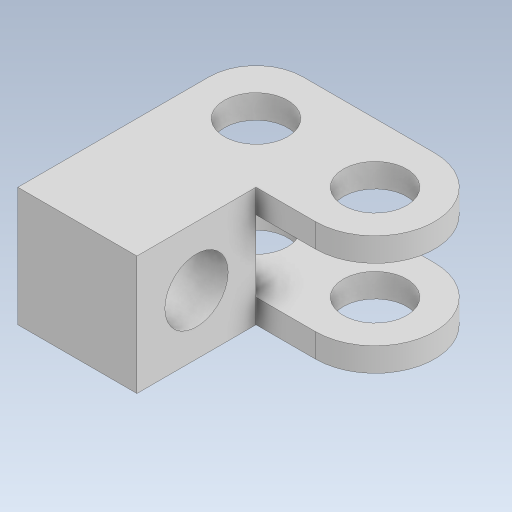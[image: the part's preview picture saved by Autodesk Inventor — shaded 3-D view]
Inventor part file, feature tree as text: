
AUTODESK INVENTOR PART (.ipt)
format: ipt  version: 2023 (Build 270158000, 158)  size: 164,864 bytes
history: native  units: in
note: dims shown in document units (in); Inventor stores cm internally (conversion verified against a paired STEP export)
features: sketch x4, extrude x2, hole x2, plane x1, fillet x1
ambient origin geometry x8: Origin, YZ Plane, XZ Plane, XY Plane, X Axis, Y Axis, Z Axis, Center Point
bodies: Solid1 (feature_tree)
feature tree (10):
  extrude  "Extrusion1"  Depth=1.0in
  sketch  "Sketch2"  dims[d2=1.0in d3=0.5in]
  extrude  "Extrusion2"  Depth=0.5in
  hole  "Hole2"  [1 undecoded]
  hole  "Hole3"  [1 undecoded]
  plane  "Work Plane1"
  fillet  "Fillet1"  [1 undecoded]
  sketch  "Sketch1"  dims[d0=0.5in d1=1.0in]
  sketch  "Sketch3"  dims[d4=0.5in d5=0.0in d6=0.25in]
  sketch  "Sketch4"  dims[d15=0.3in d16=0.5in d17=0.0in d18=0.266in d19=0.75in d20=0.375in d21=0.25in d22=0.5635in d23=0.5in d24=0.8108in d25=0.266in d26=0.75in d27=0.375in d28=0.25in d29=0.5635in d30=0.5in d31=0.8108in d32=-0.25in d35=0.1969in]
note: 3 required parameter values undecoded (feature->parameter linkage not recoverable at this tier; creation-order binding heuristic only, values carry confidence <= 0.55)
